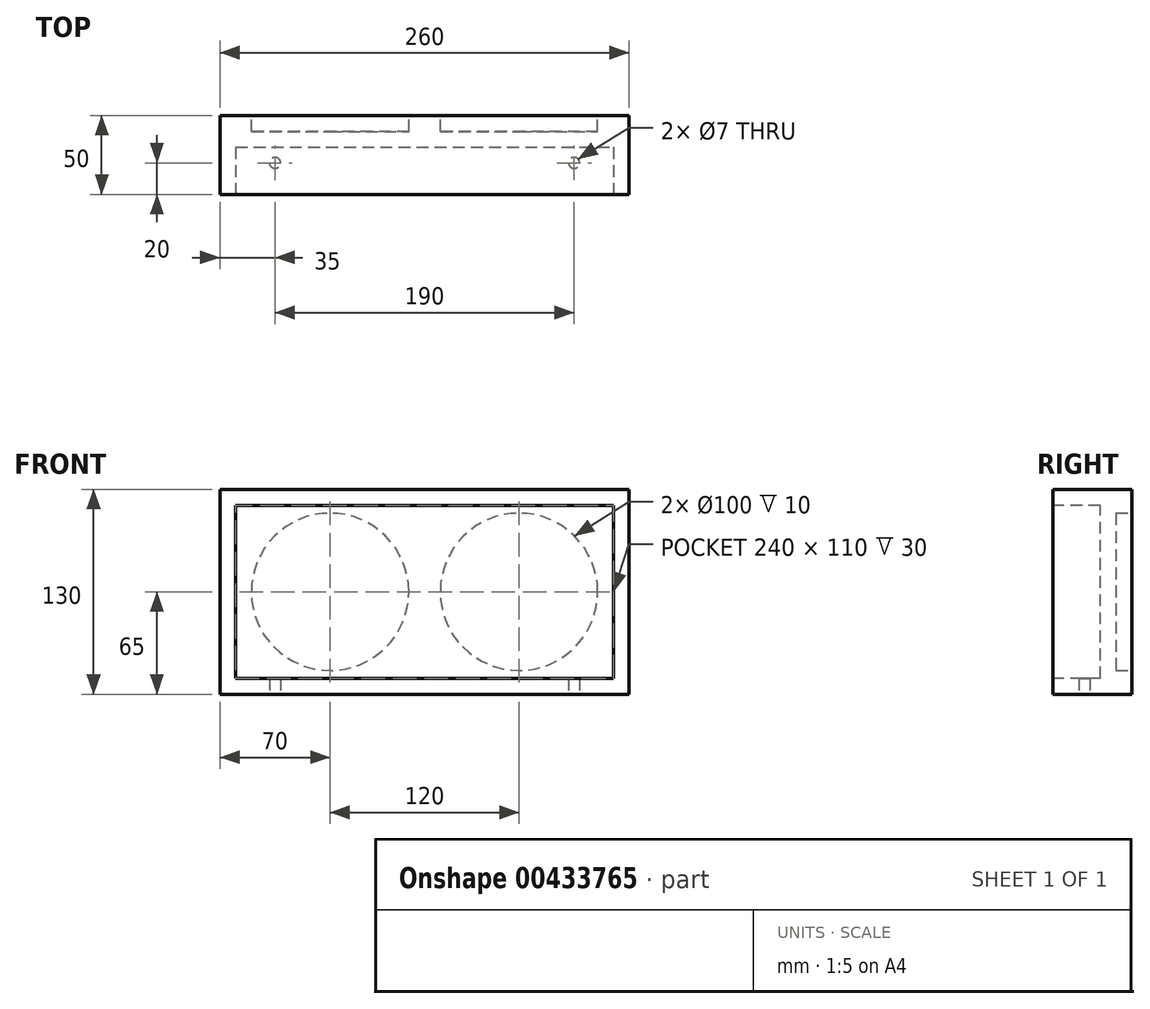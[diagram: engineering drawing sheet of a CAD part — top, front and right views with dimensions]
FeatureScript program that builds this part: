
annotation { "Feature Type Name" : "Feature", "Feature Type Description" : "" }
export const myFeature = defineFeature(function(context is Context, id is Id, definition is map)
    precondition{}
    {
        {
            var Q0;
            Q0=qCreatedBy(makeId("Front.planeOp"),FACE);
            var sketch = newSketch(context, id + "F0", { "sketchPlane" : qUnion([Q0])});
            skLineSegment(sketch, "E0.bottom", {"start": v(130, -65) * mm, "end": v(-130, -65) * mm});
            skLineSegment(sketch, "E0.top", {"start": v(130, 65) * mm, "end": v(-130, 65) * mm});
            skLineSegment(sketch, "E0.left", {"start": v(130, -65) * mm, "end": v(130, 65) * mm});
            skLineSegment(sketch, "E0.right", {"start": v(-130, -65) * mm, "end": v(-130, 65) * mm});
            skPoint(sketch, "E0.middle", {"position": v(0, 0) * mm});
            skSolve(sketch);
        }
        {
            var Q0;
            Q0=makeQuery(id+"F0.imprint","IMPRINT",FACE,{"disambiguationData":[TD([[makeQuery(id+"F0.imprint","IMPRINT",EDGE,{"derivedFrom":sQuery(id+"F0.wireOp",EDGE,"E0.bottom")}),-1.0]])]});
            extrude(context, id + "F1", {"entities" : qUnion([Q0]), "depth" : 50 * mm});
        }
        {
            var Q0;
            Q0=makeQuery(id+"F1.opExtrude","CAP_FACE",FACE,{"disambiguationData":[OSD([sQuery(id+"F0.wireOp",EDGE,"E0.bottom"),sQuery(id+"F0.wireOp",EDGE,"E0.top"),sQuery(id+"F0.wireOp",EDGE,"E0.left"),sQuery(id+"F0.wireOp",EDGE,"E0.right")])],"isStart":true});
            var sketch = newSketch(context, id + "F2", { "sketchPlane" : qUnion([Q0])});
            skCircle(sketch, "E1", {"center": v(60, 0) * mm, "radius": 50 * mm});
            skCircle(sketch, "E2", {"center": v(-60, 0) * mm, "radius": 50 * mm});
            skSolve(sketch);
        }
        {
            var Q0;
            Q0=makeQuery(id+"F2.imprint","IMPRINT",FACE,{"disambiguationData":[TD([[makeQuery(id+"F2.imprint","IMPRINT",EDGE,{"derivedFrom":sQuery(id+"F2.wireOp",EDGE,"E1")}),1.0]])]});
            var Q1;
            Q1=makeQuery(id+"F2.imprint","IMPRINT",FACE,{"disambiguationData":[TD([[makeQuery(id+"F2.imprint","IMPRINT",EDGE,{"derivedFrom":sQuery(id+"F2.wireOp",EDGE,"E2")}),1.0]])]});
            extrude(context, id + "F3", {"entities" : qUnion([Q0, Q1]), "operationType" : NewBodyOperationType.REMOVE, "oppositeDirection" : true, "depth" : 10 * mm});
        }
        {
            var Q0;
            Q0=makeQuery(id+"F1.opExtrude","CAP_FACE",FACE,{"disambiguationData":[OSD([sQuery(id+"F0.wireOp",EDGE,"E0.bottom"),sQuery(id+"F0.wireOp",EDGE,"E0.top"),sQuery(id+"F0.wireOp",EDGE,"E0.left"),sQuery(id+"F0.wireOp",EDGE,"E0.right")])],"isStart":false});
            var sketch = newSketch(context, id + "F4", { "sketchPlane" : qUnion([Q0])});
            skLineSegment(sketch, "E3.bottom", {"start": v(-120, -55) * mm, "end": v(120, -55) * mm});
            skLineSegment(sketch, "E3.top", {"start": v(-120, 55) * mm, "end": v(120, 55) * mm});
            skLineSegment(sketch, "E3.left", {"start": v(-120, -55) * mm, "end": v(-120, 55) * mm});
            skLineSegment(sketch, "E3.right", {"start": v(120, -55) * mm, "end": v(120, 55) * mm});
            skPoint(sketch, "E3.middle", {"position": v(0, 0) * mm});
            skSolve(sketch);
        }
        {
            var Q0;
            Q0=makeQuery(id+"F4.imprint","IMPRINT",FACE,{"disambiguationData":[TD([[makeQuery(id+"F4.imprint","IMPRINT",EDGE,{"derivedFrom":sQuery(id+"F4.wireOp",EDGE,"E3.bottom")}),1.0]])]});
            extrude(context, id + "F5", {"entities" : qUnion([Q0]), "operationType" : NewBodyOperationType.REMOVE, "oppositeDirection" : true, "depth" : 30 * mm});
        }
        {
            var Q0;
            Q0=makeQuery(id+"F1.opExtrude","SWEPT_FACE",FACE,{"disambiguationData":[OSD([sQuery(id+"F0.wireOp",EDGE,"E0.bottom")])]});
            var sketch = newSketch(context, id + "F6", { "sketchPlane" : qUnion([Q0])});
            skCircle(sketch, "E4", {"center": v(95, 30) * mm, "radius": 3.5 * mm});
            skCircle(sketch, "E5", {"center": v(-95, 30) * mm, "radius": 3.5 * mm});
            skSolve(sketch);
        }
        {
            var Q0;
            Q0=makeQuery(id+"F6.imprint","IMPRINT",FACE,{"disambiguationData":[TD([[makeQuery(id+"F6.imprint","IMPRINT",EDGE,{"derivedFrom":sQuery(id+"F6.wireOp",EDGE,"E4")}),1.0]])]});
            var Q1;
            Q1=makeQuery(id+"F6.imprint","IMPRINT",FACE,{"disambiguationData":[TD([[makeQuery(id+"F6.imprint","IMPRINT",EDGE,{"derivedFrom":sQuery(id+"F6.wireOp",EDGE,"E5")}),1.0]])]});
            extrude(context, id + "F7", {"entities" : qUnion([Q0, Q1]), "operationType" : NewBodyOperationType.REMOVE, "oppositeDirection" : true, "depth" : 50 * mm});
        }
    });
